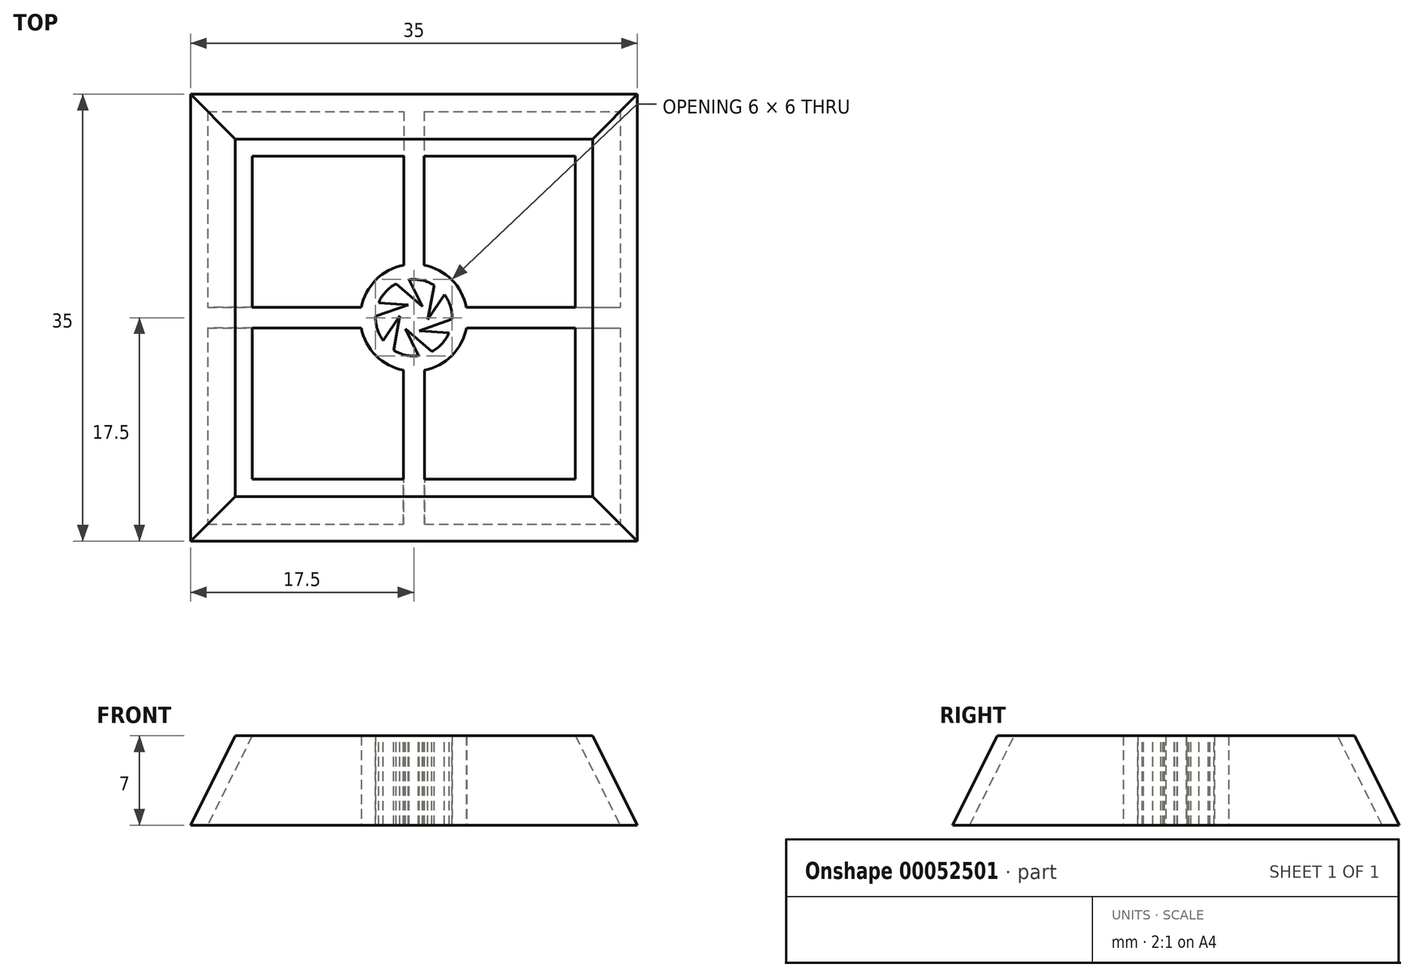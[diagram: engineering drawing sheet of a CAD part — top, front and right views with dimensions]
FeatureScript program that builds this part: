
annotation { "Feature Type Name" : "Feature", "Feature Type Description" : "" }
export const myFeature = defineFeature(function(context is Context, id is Id, definition is map)
    precondition{}
    {
        {
            var Q0;
            Q0=qCreatedBy(makeId("Top.planeOp"),FACE);
            var sketch = newSketch(context, id + "F0", { "sketchPlane" : qUnion([Q0])});
            skLineSegment(sketch, "E0.rect.bottom", {"start": v(-17.5, 17.5) * mm, "end": v(17.5, 17.5) * mm});
            skLineSegment(sketch, "E0.rect.top", {"start": v(-17.5, -17.5) * mm, "end": v(17.5, -17.5) * mm});
            skLineSegment(sketch, "E0.rect.left", {"start": v(-17.5, 17.5) * mm, "end": v(-17.5, -17.5) * mm});
            skLineSegment(sketch, "E0.rect.right", {"start": v(17.5, 17.5) * mm, "end": v(17.5, -17.5) * mm});
            skPoint(sketch, "E0.rect.middle", {"position": v(0, 0) * mm});
            skSolve(sketch);
        }
        {
            var Q0;
            Q0=qCreatedBy(makeId("Top.planeOp"),FACE);
            cPlane(context, id + "F1", {"entities" : qUnion([Q0]), "cplaneType" : CPlaneType.OFFSET, "offset" : 7 * mm, "width" : 150 * mm, "height" : 150 * mm});
        }
        {
            var Q0;
            Q0=qCreatedBy(id+"F1.planeOp",FACE);
            var sketch = newSketch(context, id + "F2", { "sketchPlane" : qUnion([Q0])});
            skLineSegment(sketch, "E1.rect.bottom", {"start": v(14, -14) * mm, "end": v(-14, -14) * mm});
            skLineSegment(sketch, "E1.rect.top", {"start": v(14, 14) * mm, "end": v(-14, 14) * mm});
            skLineSegment(sketch, "E1.rect.left", {"start": v(14, -14) * mm, "end": v(14, 14) * mm});
            skLineSegment(sketch, "E1.rect.right", {"start": v(-14, -14) * mm, "end": v(-14, 14) * mm});
            skPoint(sketch, "E1.rect.middle", {"position": v(0, 0) * mm});
            skSolve(sketch);
        }
        {
            var Q0;
            Q0=makeQuery(id+"F0.imprint","IMPRINT",FACE,{"disambiguationData":[TD([[makeQuery(id+"F0.imprint","IMPRINT",EDGE,{"derivedFrom":sQuery(id+"F0.wireOp",EDGE,"E0.rect.bottom")}),-1.0]])]});
            var Q1;
            Q1=makeQuery(id+"F2.imprint","IMPRINT",FACE,{"disambiguationData":[TD([[makeQuery(id+"F2.imprint","IMPRINT",EDGE,{"derivedFrom":sQuery(id+"F2.wireOp",EDGE,"E1.rect.bottom")}),-1.0]])]});
            loft(context, id + "F3", {"sheetProfilesArray" : [{ "sheetProfileEntities" : qUnion([Q0]) }, { "sheetProfileEntities" : qUnion([Q1]) }]});
        }
        {
            var Q0;
            Q0=makeQuery(id+"F3.opLoft","CAP_FACE",FACE,{"disambiguationData":[OSD([makeQuery(id+"F2.imprint","IMPRINT",FACE,{"disambiguationData":[TD([[makeQuery(id+"F2.imprint","IMPRINT",EDGE,{"derivedFrom":sQuery(id+"F2.wireOp",EDGE,"E1.rect.bottom")}),-1.0]])]})])],"isStart":true});
            var Q1;
            Q1=makeQuery(id+"F3.opLoft","CAP_FACE",FACE,{"disambiguationData":[OSD([makeQuery(id+"F0.imprint","IMPRINT",FACE,{"disambiguationData":[TD([[makeQuery(id+"F0.imprint","IMPRINT",EDGE,{"derivedFrom":sQuery(id+"F0.wireOp",EDGE,"E0.rect.bottom")}),-1.0]])]})])],"isStart":true});
            shell(context, id + "F4", {"entities" : qUnion([Q0, Q1]), "thickness" : 1.2 * mm});
        }
        {
            var Q0;
            Q0=qCreatedBy(makeId("Top.planeOp"),FACE);
            var sketch = newSketch(context, id + "F5", { "sketchPlane" : qUnion([Q0])});
            skLineSegment(sketch, "E2.0", {"start": v(17.5, 17.5) * mm, "end": v(-17.5, 17.5) * mm, "construction": true});
            skLineSegment(sketch, "E2.1", {"start": v(-17.5, -17.5) * mm, "end": v(17.5, -17.5) * mm, "construction": true});
            skLineSegment(sketch, "E2.2", {"start": v(17.5, -17.5) * mm, "end": v(17.5, 17.5) * mm, "construction": true});
            skLineSegment(sketch, "E2.3", {"start": v(-17.5, 17.5) * mm, "end": v(-17.5, -17.5) * mm, "construction": true});
            skCircle(sketch, "E3", {"center": v(0, 0) * mm, "radius": 3 * mm});
            skArc(sketch, "E4.0", {"start": v(-4.12, -0.8) * mm, "mid": v(-2.98, -2.96) * mm, "end": v(-0.82, -4.12) * mm});
            skLineSegment(sketch, "E5", {"start": v(0, 17.5) * mm, "end": v(0, -17.5) * mm, "construction": true});
            skLineSegment(sketch, "E6", {"start": v(-17.5, 0) * mm, "end": v(17.5, 0) * mm, "construction": true});
            skLineSegment(sketch, "E7", {"start": v(-0.8, 16.2) * mm, "end": v(-0.8, 4.12) * mm});
            skLineSegment(sketch, "E8.MirrorCS", {"start": v(0.8, 16.2) * mm, "end": v(0.8, 4.12) * mm});
            skLineSegment(sketch, "E9", {"start": v(-16.2, -0.8) * mm, "end": v(-4.12, -0.8) * mm});
            skLineSegment(sketch, "E10.MirrorCS", {"start": v(-16.2, 0.8) * mm, "end": v(-4.12, 0.8) * mm});
            skLineSegment(sketch, "E11", {"start": v(-17.5, 0.8) * mm, "end": v(-17.5, -0.8) * mm});
            skLineSegment(sketch, "E12", {"start": v(17.5, 0.8) * mm, "end": v(17.5, -0.8) * mm});
            skLineSegment(sketch, "E13", {"start": v(-0.8, -17.5) * mm, "end": v(0.8, -17.5) * mm});
            skLineSegment(sketch, "E14", {"start": v(-0.8, 17.5) * mm, "end": v(0.8, 17.5) * mm});
            skLineSegment(sketch, "E15.rect.bottom", {"start": v(-16.2, 16.2) * mm, "end": v(16.2, 16.2) * mm, "construction": true});
            skLineSegment(sketch, "E15.rect.top", {"start": v(-16.2, -16.2) * mm, "end": v(16.2, -16.2) * mm, "construction": true});
            skLineSegment(sketch, "E15.rect.left", {"start": v(-16.2, 16.2) * mm, "end": v(-16.2, -16.2) * mm, "construction": true});
            skLineSegment(sketch, "E15.rect.right", {"start": v(16.2, 16.2) * mm, "end": v(16.2, -16.2) * mm, "construction": true});
            skLineSegment(sketch, "E16", {"start": v(-0.82, -16.2) * mm, "end": v(0.82, -16.2) * mm});
            skLineSegment(sketch, "E17", {"start": v(16.2, 0.82) * mm, "end": v(16.2, -0.8) * mm});
            skLineSegment(sketch, "E18", {"start": v(-0.8, 16.2) * mm, "end": v(0.8, 16.2) * mm});
            skLineSegment(sketch, "E19", {"start": v(-16.2, -0.8) * mm, "end": v(-16.2, 0.8) * mm});
            skLineSegment(sketch, "E20.trimOffspring", {"start": v(4.12, -0.8) * mm, "end": v(16.2, -0.8) * mm});
            skLineSegment(sketch, "E21.trimOffspring", {"start": v(4.12, 0.82) * mm, "end": v(16.2, 0.82) * mm});
            skLineSegment(sketch, "E22.trimOffspring", {"start": v(-0.82, -4.12) * mm, "end": v(-0.82, -16.2) * mm});
            skLineSegment(sketch, "E23.trimOffspring", {"start": v(0.82, -4.12) * mm, "end": v(0.82, -16.2) * mm});
            skArc(sketch, "E24.trimOffspring", {"start": v(4.12, 0.82) * mm, "mid": v(2.96, 2.98) * mm, "end": v(0.8, 4.12) * mm});
            skArc(sketch, "E25.trimOffspring", {"start": v(0.82, -4.12) * mm, "mid": v(2.98, -2.96) * mm, "end": v(4.12, -0.8) * mm});
            skArc(sketch, "E26.trimOffspring", {"start": v(-0.8, 4.12) * mm, "mid": v(-2.97, 2.97) * mm, "end": v(-4.12, 0.8) * mm});
            skSolve(sketch);
        }
        {
            var Q0;
            {var subQ5=sQuery(id+"F5.wireOp",EDGE,"E19");Q0=makeQuery(id+"F5.imprint","IMPRINT",FACE,{"disambiguationData":[TD([[makeQuery(id+"F5.imprint","IMPRINT",EDGE,{"derivedFrom":subQ5}),-1.0]])]});}
            var Q1;
            {var subQ0=sQuery(id+"F5.wireOp",EDGE,"E10.MirrorCS");var subQ1=sQuery(id+"F5.wireOp",EDGE,"E3");var subQ2=makeQuery(id+"F5.imprint","INTERSECT",VERTEX,{"disambiguationData":[OD(1.0)],"derivedFrom":[subQ1,subQ0]});Q1=makeQuery(id+"F5.imprint","IMPRINT",FACE,{"disambiguationData":[TD([[makeQuery(id+"F5.imprint","IMPRINT",EDGE,{"disambiguationData":[TD([[subQ2,-1.0]])],"derivedFrom":subQ1}),-1.0]])]});}
            var Q2;
            {var subQ0=sQuery(id+"F5.wireOp",EDGE,"E7");var subQ1=sQuery(id+"F5.wireOp",EDGE,"E3");var subQ2=makeQuery(id+"F5.imprint","INTERSECT",VERTEX,{"disambiguationData":[OD(0.0)],"derivedFrom":[subQ1,subQ0]});Q2=makeQuery(id+"F5.imprint","IMPRINT",FACE,{"disambiguationData":[TD([[makeQuery(id+"F5.imprint","IMPRINT",EDGE,{"disambiguationData":[TD([[subQ2,-1.0]])],"derivedFrom":subQ1}),-1.0]])]});}
            var Q3;
            {var subQ0=sQuery(id+"F5.wireOp",EDGE,"E8.MirrorCS");var subQ1=sQuery(id+"F5.wireOp",EDGE,"E3");var subQ2=makeQuery(id+"F5.imprint","INTERSECT",VERTEX,{"disambiguationData":[OD(0.0)],"derivedFrom":[subQ1,subQ0]});Q3=makeQuery(id+"F5.imprint","IMPRINT",FACE,{"disambiguationData":[TD([[makeQuery(id+"F5.imprint","IMPRINT",EDGE,{"disambiguationData":[TD([[subQ2,-1.0]])],"derivedFrom":subQ1}),-1.0]])]});}
            var Q4;
            {var subQ5=sQuery(id+"F5.wireOp",EDGE,"E18");Q4=makeQuery(id+"F5.imprint","IMPRINT",FACE,{"disambiguationData":[TD([[makeQuery(id+"F5.imprint","IMPRINT",EDGE,{"derivedFrom":subQ5}),-1.0]])]});}
            var Q5;
            {var subQ0=sQuery(id+"F5.wireOp",EDGE,"E8.MirrorCS");var subQ1=sQuery(id+"F5.wireOp",EDGE,"E3");var subQ2=makeQuery(id+"F5.imprint","INTERSECT",VERTEX,{"disambiguationData":[OD(0.0)],"derivedFrom":[subQ1,subQ0]});Q5=makeQuery(id+"F5.imprint","IMPRINT",FACE,{"disambiguationData":[TD([[makeQuery(id+"F5.imprint","IMPRINT",EDGE,{"disambiguationData":[TD([[subQ2,1.0]])],"derivedFrom":subQ1}),-1.0]])]});}
            var Q6;
            {var subQ0=sQuery(id+"F5.wireOp",EDGE,"E10.MirrorCS");var subQ1=sQuery(id+"F5.wireOp",EDGE,"E3");var subQ2=makeQuery(id+"F5.imprint","INTERSECT",VERTEX,{"disambiguationData":[OD(0.0)],"derivedFrom":[subQ1,subQ0]});Q6=makeQuery(id+"F5.imprint","IMPRINT",FACE,{"disambiguationData":[TD([[makeQuery(id+"F5.imprint","IMPRINT",EDGE,{"disambiguationData":[TD([[subQ2,1.0]])],"derivedFrom":subQ1}),-1.0]])]});}
            var Q7;
            {var subQ5=sQuery(id+"F5.wireOp",EDGE,"E17");Q7=makeQuery(id+"F5.imprint","IMPRINT",FACE,{"disambiguationData":[TD([[makeQuery(id+"F5.imprint","IMPRINT",EDGE,{"derivedFrom":subQ5}),-1.0]])]});}
            var Q8;
            {var subQ0=sQuery(id+"F5.wireOp",EDGE,"E8.MirrorCS");var subQ1=sQuery(id+"F5.wireOp",EDGE,"E3");var subQ2=makeQuery(id+"F5.imprint","INTERSECT",VERTEX,{"disambiguationData":[OD(1.0)],"derivedFrom":[subQ1,subQ0]});Q8=makeQuery(id+"F5.imprint","IMPRINT",FACE,{"disambiguationData":[TD([[makeQuery(id+"F5.imprint","IMPRINT",EDGE,{"disambiguationData":[TD([[subQ2,-1.0]])],"derivedFrom":subQ1}),-1.0]])]});}
            var Q9;
            {var subQ0=sQuery(id+"F5.wireOp",EDGE,"E9");var subQ1=sQuery(id+"F5.wireOp",EDGE,"E3");var subQ2=makeQuery(id+"F5.imprint","INTERSECT",VERTEX,{"disambiguationData":[OD(0.0)],"derivedFrom":[subQ1,subQ0]});Q9=makeQuery(id+"F5.imprint","IMPRINT",FACE,{"disambiguationData":[TD([[makeQuery(id+"F5.imprint","IMPRINT",EDGE,{"disambiguationData":[TD([[subQ2,-1.0]])],"derivedFrom":subQ1}),-1.0]])]});}
            var Q10;
            {var subQ0=sQuery(id+"F5.wireOp",EDGE,"E7");var subQ1=sQuery(id+"F5.wireOp",EDGE,"E3");var subQ2=makeQuery(id+"F5.imprint","INTERSECT",VERTEX,{"disambiguationData":[OD(1.0)],"derivedFrom":[subQ1,subQ0]});Q10=makeQuery(id+"F5.imprint","IMPRINT",FACE,{"disambiguationData":[TD([[makeQuery(id+"F5.imprint","IMPRINT",EDGE,{"disambiguationData":[TD([[subQ2,-1.0]])],"derivedFrom":subQ1}),-1.0]])]});}
            var Q11;
            {var subQ5=sQuery(id+"F5.wireOp",EDGE,"E16");Q11=makeQuery(id+"F5.imprint","IMPRINT",FACE,{"disambiguationData":[TD([[makeQuery(id+"F5.imprint","IMPRINT",EDGE,{"derivedFrom":subQ5}),1.0]])]});}
            var Q12;
            Q12=makeQuery(id+"F3.opLoft","CAP_FACE",FACE,{"disambiguationData":[OSD([makeQuery(id+"F2.imprint","IMPRINT",FACE,{"disambiguationData":[TD([[makeQuery(id+"F2.imprint","IMPRINT",EDGE,{"derivedFrom":sQuery(id+"F2.wireOp",EDGE,"E1.rect.bottom")}),-1.0]])]})])],"isStart":true});
            extrude(context, id + "F6", {"entities" : qUnion([Q0, Q1, Q2, Q3, Q4, Q5, Q6, Q7, Q8, Q9, Q10, Q11]), "endBound" : BoundingType.UP_TO_SURFACE, "endBoundEntityFace" : qUnion([Q12]), "depth" : 8.93 * mm});
        }
        {
            var Q0;
            Q0=makeQuery(id+"F6.opExtrude","CAP_EDGE",EDGE,{"disambiguationData":[OSD([sQuery(id+"F5.wireOp",EDGE,"E19")])],"isStart":false});
            var Q1;
            Q1=makeQuery(id+"F6.opExtrude","CAP_EDGE",EDGE,{"disambiguationData":[OSD([sQuery(id+"F5.wireOp",EDGE,"E18")])],"isStart":false});
            var Q2;
            Q2=makeQuery(id+"F6.opExtrude","CAP_EDGE",EDGE,{"disambiguationData":[OSD([sQuery(id+"F5.wireOp",EDGE,"E17")])],"isStart":false});
            var Q3;
            Q3=makeQuery(id+"F6.opExtrude","CAP_EDGE",EDGE,{"disambiguationData":[OSD([sQuery(id+"F5.wireOp",EDGE,"E16")])],"isStart":false});
            chamfer(context, id + "F7", {"entities" : qUnion([Q0, Q1, Q2, Q3]), "chamferType" : ChamferType.TWO_OFFSETS, "width1" : 6 * mm, "oppositeDirection" : false, "width2" : 3 * mm, "tangentPropagation" : true});
        }
        {
            var Q0;
            Q0=makeQuery(id+"F3.opLoft","SWEPT_BODY",BODY,{"disambiguationData":[OSD([makeQuery(id+"F0.imprint","IMPRINT",FACE,{"disambiguationData":[TD([[makeQuery(id+"F0.imprint","IMPRINT",EDGE,{"derivedFrom":sQuery(id+"F0.wireOp",EDGE,"E0.rect.bottom")}),-1.0]])]}),makeQuery(id+"F2.imprint","IMPRINT",FACE,{"disambiguationData":[TD([[makeQuery(id+"F2.imprint","IMPRINT",EDGE,{"derivedFrom":sQuery(id+"F2.wireOp",EDGE,"E1.rect.bottom")}),-1.0]])]})])]});
            var Q1;
            Q1=makeQuery(id+"F6.opExtrude","SWEPT_BODY",BODY,{"disambiguationData":[OSD([sQuery(id+"F5.wireOp",EDGE,"E3"),sQuery(id+"F5.wireOp",EDGE,"E4.0"),sQuery(id+"F5.wireOp",EDGE,"E7"),sQuery(id+"F5.wireOp",EDGE,"E8.MirrorCS"),sQuery(id+"F5.wireOp",EDGE,"E9"),sQuery(id+"F5.wireOp",EDGE,"E10.MirrorCS"),sQuery(id+"F5.wireOp",EDGE,"E16"),sQuery(id+"F5.wireOp",EDGE,"E17"),sQuery(id+"F5.wireOp",EDGE,"E18"),sQuery(id+"F5.wireOp",EDGE,"E19"),sQuery(id+"F5.wireOp",EDGE,"E20.trimOffspring"),sQuery(id+"F5.wireOp",EDGE,"E21.trimOffspring"),sQuery(id+"F5.wireOp",EDGE,"E22.trimOffspring"),sQuery(id+"F5.wireOp",EDGE,"E23.trimOffspring"),sQuery(id+"F5.wireOp",EDGE,"E24.trimOffspring"),sQuery(id+"F5.wireOp",EDGE,"E25.trimOffspring"),sQuery(id+"F5.wireOp",EDGE,"E26.trimOffspring")])]});
            booleanBodies(context, id + "F8", {"operationType" : BooleanOperationType.UNION, "tools" : qUnion([Q0, Q1])});
        }
        {
            var Q0;
            Q0=makeQuery(id+"F8.opBoolean","MERGE",FACE,{"derivedFrom":[makeQuery(id+"F3.opLoft","CAP_FACE",FACE,{"disambiguationData":[OSD([makeQuery(id+"F2.imprint","IMPRINT",FACE,{"disambiguationData":[TD([[makeQuery(id+"F2.imprint","IMPRINT",EDGE,{"derivedFrom":sQuery(id+"F2.wireOp",EDGE,"E1.rect.bottom")}),-1.0]])]})])],"isStart":true}),makeQuery(id+"F6.opExtrude","CAP_FACE",FACE,{"disambiguationData":[OSD([sQuery(id+"F5.wireOp",EDGE,"E3"),sQuery(id+"F5.wireOp",EDGE,"E4.0"),sQuery(id+"F5.wireOp",EDGE,"E7"),sQuery(id+"F5.wireOp",EDGE,"E8.MirrorCS"),sQuery(id+"F5.wireOp",EDGE,"E9"),sQuery(id+"F5.wireOp",EDGE,"E10.MirrorCS"),sQuery(id+"F5.wireOp",EDGE,"E16"),sQuery(id+"F5.wireOp",EDGE,"E17"),sQuery(id+"F5.wireOp",EDGE,"E18"),sQuery(id+"F5.wireOp",EDGE,"E19"),sQuery(id+"F5.wireOp",EDGE,"E20.trimOffspring"),sQuery(id+"F5.wireOp",EDGE,"E21.trimOffspring"),sQuery(id+"F5.wireOp",EDGE,"E22.trimOffspring"),sQuery(id+"F5.wireOp",EDGE,"E23.trimOffspring"),sQuery(id+"F5.wireOp",EDGE,"E24.trimOffspring"),sQuery(id+"F5.wireOp",EDGE,"E25.trimOffspring"),sQuery(id+"F5.wireOp",EDGE,"E26.trimOffspring")])],"isStart":false})]});
            var sketch = newSketch(context, id + "F9", { "sketchPlane" : qUnion([Q0])});
            skLineSegment(sketch, "E27", {"start": v(0, 3.43) * mm, "end": v(0, 0) * mm, "construction": true});
            skLineSegment(sketch, "E28", {"start": v(-0.36, 2.98) * mm, "end": v(0.66, 0.88) * mm});
            skLineSegment(sketch, "E29", {"start": v(0.66, 0.88) * mm, "end": v(-1.4, 2.65) * mm});
            skArc(sketch, "E30", {"start": v(-0.36, 2.98) * mm, "mid": v(-0.9, 2.9) * mm, "end": v(-1.4, 2.65) * mm});
            skArc(sketch, "E31.1.0", {"start": v(-2.76, 1.18) * mm, "mid": v(-2.96, 0.66) * mm, "end": v(-3, 0.1) * mm});
            skLineSegment(sketch, "E31.1.1", {"start": v(-0.43, 1.01) * mm, "end": v(-3, 0.1) * mm});
            skLineSegment(sketch, "E31.1.2", {"start": v(-2.76, 1.18) * mm, "end": v(-0.43, 1.01) * mm});
            skArc(sketch, "E31.2.0", {"start": v(-2.4, -1.8) * mm, "mid": v(-2.05, -2.23) * mm, "end": v(-1.6, -2.54) * mm});
            skLineSegment(sketch, "E31.2.1", {"start": v(-1.1, 0.13) * mm, "end": v(-1.6, -2.54) * mm});
            skLineSegment(sketch, "E31.2.2", {"start": v(-2.4, -1.8) * mm, "end": v(-1.1, 0.13) * mm});
            skArc(sketch, "E31.3.0", {"start": v(0.36, -2.98) * mm, "mid": v(0.9, -2.9) * mm, "end": v(1.4, -2.65) * mm});
            skLineSegment(sketch, "E31.3.1", {"start": v(-0.66, -0.88) * mm, "end": v(1.4, -2.65) * mm});
            skLineSegment(sketch, "E31.3.2", {"start": v(0.36, -2.98) * mm, "end": v(-0.66, -0.88) * mm});
            skArc(sketch, "E31.4.0", {"start": v(2.76, -1.18) * mm, "mid": v(2.96, -0.66) * mm, "end": v(3, -0.1) * mm});
            skLineSegment(sketch, "E31.4.1", {"start": v(0.43, -1.01) * mm, "end": v(3, -0.1) * mm});
            skLineSegment(sketch, "E31.4.2", {"start": v(2.76, -1.18) * mm, "end": v(0.43, -1.01) * mm});
            skPoint(sketch, "E31.center", {"position": v(0, 0) * mm});
            skCircle(sketch, "E32", {"center": v(0, 0) * mm, "radius": 1.1 * mm, "construction": true});
            skArc(sketch, "E33.1.5.0", {"start": v(2.4, 1.8) * mm, "mid": v(2.05, 2.23) * mm, "end": v(1.6, 2.54) * mm});
            skLineSegment(sketch, "E33.4.5.0", {"start": v(1.1, -0.13) * mm, "end": v(1.6, 2.54) * mm});
            skLineSegment(sketch, "E33.7.5.0", {"start": v(2.4, 1.8) * mm, "end": v(1.1, -0.13) * mm});
            skSolve(sketch);
        }
        {
            var Q0;
            {var subQ0=sQuery(id+"F9.wireOp",EDGE,"E28");Q0=makeQuery(id+"F9.imprint","IMPRINT",FACE,{"disambiguationData":[TD([[makeQuery(id+"F9.imprint","IMPRINT",EDGE,{"derivedFrom":subQ0}),-1.0]])]});}
            var Q1;
            {var subQ0=sQuery(id+"F9.wireOp",EDGE,"E31.1.1");Q1=makeQuery(id+"F9.imprint","IMPRINT",FACE,{"disambiguationData":[TD([[makeQuery(id+"F9.imprint","IMPRINT",EDGE,{"derivedFrom":subQ0}),-1.0]])]});}
            var Q2;
            {var subQ0=sQuery(id+"F9.wireOp",EDGE,"E31.2.1");Q2=makeQuery(id+"F9.imprint","IMPRINT",FACE,{"disambiguationData":[TD([[makeQuery(id+"F9.imprint","IMPRINT",EDGE,{"derivedFrom":subQ0}),-1.0]])]});}
            var Q3;
            {var subQ0=sQuery(id+"F9.wireOp",EDGE,"E31.3.1");Q3=makeQuery(id+"F9.imprint","IMPRINT",FACE,{"disambiguationData":[TD([[makeQuery(id+"F9.imprint","IMPRINT",EDGE,{"derivedFrom":subQ0}),-1.0]])]});}
            var Q4;
            {var subQ0=sQuery(id+"F9.wireOp",EDGE,"E31.4.1");Q4=makeQuery(id+"F9.imprint","IMPRINT",FACE,{"disambiguationData":[TD([[makeQuery(id+"F9.imprint","IMPRINT",EDGE,{"derivedFrom":subQ0}),-1.0]])]});}
            var Q5;
            {var subQ0=sQuery(id+"F9.wireOp",EDGE,"E33.4.5.0");Q5=makeQuery(id+"F9.imprint","IMPRINT",FACE,{"disambiguationData":[TD([[makeQuery(id+"F9.imprint","IMPRINT",EDGE,{"derivedFrom":subQ0}),-1.0]])]});}
            var Q6;
            Q6=makeQuery(id+"F8.opBoolean","MERGE",FACE,{"derivedFrom":[makeQuery(id+"F3.opLoft","CAP_FACE",FACE,{"disambiguationData":[OSD([makeQuery(id+"F0.imprint","IMPRINT",FACE,{"disambiguationData":[TD([[makeQuery(id+"F0.imprint","IMPRINT",EDGE,{"derivedFrom":sQuery(id+"F0.wireOp",EDGE,"E0.rect.bottom")}),-1.0]])]})])],"isStart":true}),makeQuery(id+"F6.opExtrude","CAP_FACE",FACE,{"disambiguationData":[OSD([sQuery(id+"F5.wireOp",EDGE,"E3"),sQuery(id+"F5.wireOp",EDGE,"E4.0"),sQuery(id+"F5.wireOp",EDGE,"E7"),sQuery(id+"F5.wireOp",EDGE,"E8.MirrorCS"),sQuery(id+"F5.wireOp",EDGE,"E9"),sQuery(id+"F5.wireOp",EDGE,"E10.MirrorCS"),sQuery(id+"F5.wireOp",EDGE,"E16"),sQuery(id+"F5.wireOp",EDGE,"E17"),sQuery(id+"F5.wireOp",EDGE,"E18"),sQuery(id+"F5.wireOp",EDGE,"E19"),sQuery(id+"F5.wireOp",EDGE,"E20.trimOffspring"),sQuery(id+"F5.wireOp",EDGE,"E21.trimOffspring"),sQuery(id+"F5.wireOp",EDGE,"E22.trimOffspring"),sQuery(id+"F5.wireOp",EDGE,"E23.trimOffspring"),sQuery(id+"F5.wireOp",EDGE,"E24.trimOffspring"),sQuery(id+"F5.wireOp",EDGE,"E25.trimOffspring"),sQuery(id+"F5.wireOp",EDGE,"E26.trimOffspring")])],"isStart":true})]});
            extrude(context, id + "F10", {"entities" : qUnion([Q0, Q1, Q2, Q3, Q4, Q5]), "operationType" : NewBodyOperationType.ADD, "endBound" : BoundingType.UP_TO_SURFACE, "oppositeDirection" : true, "endBoundEntityFace" : qUnion([Q6]), "depth" : 25 * mm});
        }
    });
